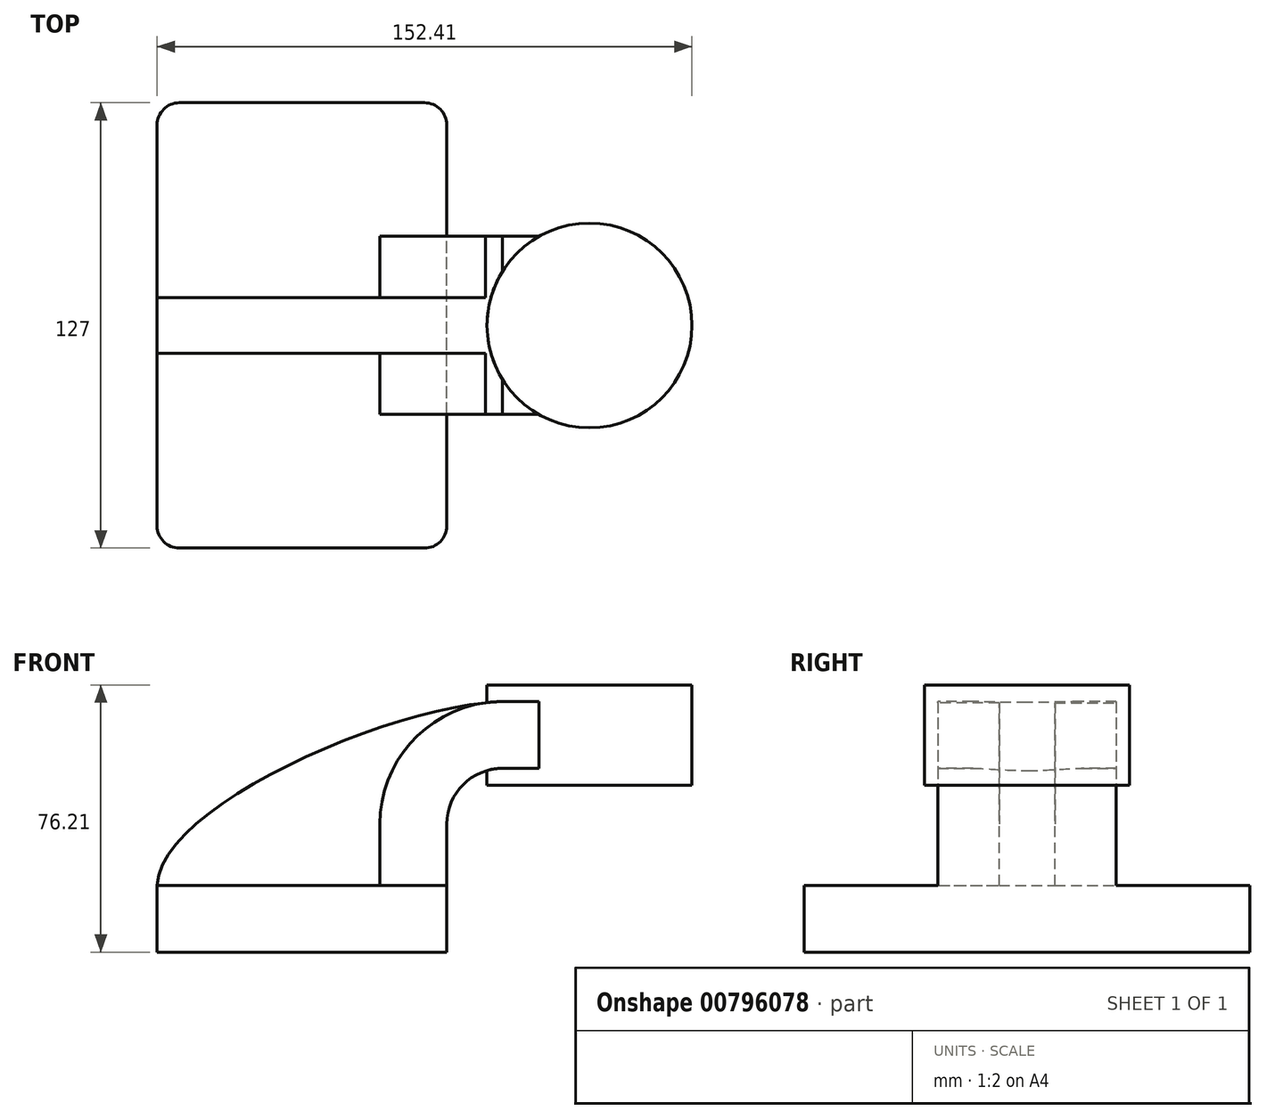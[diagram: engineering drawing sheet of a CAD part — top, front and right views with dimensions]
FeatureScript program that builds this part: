
annotation { "Feature Type Name" : "Feature", "Feature Type Description" : "" }
export const myFeature = defineFeature(function(context is Context, id is Id, definition is map)
    precondition{}
    {
        {
            var Q0;
            Q0=qCreatedBy(makeId("Front.planeOp"),FACE);
            var sketch = newSketch(context, id + "F0", { "sketchPlane" : qUnion([Q0])});
            skLineSegment(sketch, "E0.bottom", {"start": v(-41.27, -9.52) * mm, "end": v(41.28, -9.52) * mm});
            skLineSegment(sketch, "E0.top", {"start": v(-41.27, 9.52) * mm, "end": v(41.28, 9.52) * mm});
            skLineSegment(sketch, "E0.left", {"start": v(-41.27, -9.52) * mm, "end": v(-41.27, 9.52) * mm});
            skLineSegment(sketch, "E0.right", {"start": v(41.28, -9.52) * mm, "end": v(41.28, 9.52) * mm});
            skPoint(sketch, "E0.middle", {"position": v(0, 0) * mm});
            skLineSegment(sketch, "E1.bottom", {"start": v(60.33, 38.1) * mm, "end": v(111.13, 38.1) * mm});
            skLineSegment(sketch, "E1.top", {"start": v(60.33, 66.68) * mm, "end": v(111.13, 66.68) * mm});
            skLineSegment(sketch, "E1.left", {"start": v(60.33, 38.1) * mm, "end": v(60.33, 66.68) * mm});
            skLineSegment(sketch, "E1.right", {"start": v(111.13, 38.1) * mm, "end": v(111.13, 66.68) * mm});
            skPoint(sketch, "E1.middle", {"position": v(85.72, 52.39) * mm});
            skLineSegment(sketch, "E2", {"start": v(41.27, 9.52) * mm, "end": v(41.27, 27) * mm});
            skArc(sketch, "E3", {"start": v(41.27, 27) * mm, "mid": v(45.92, 38.23) * mm, "end": v(57.15, 42.88) * mm});
            skLineSegment(sketch, "E4", {"start": v(57.15, 42.88) * mm, "end": v(81.93, 42.88) * mm});
            skLineSegment(sketch, "E5.0", {"start": v(57.15, 61.93) * mm, "end": v(81.93, 61.93) * mm});
            skArc(sketch, "E5.1", {"start": v(22.22, 27) * mm, "mid": v(32.45, 51.7) * mm, "end": v(57.15, 61.93) * mm});
            skLineSegment(sketch, "E5.2", {"start": v(22.22, 9.52) * mm, "end": v(22.22, 27) * mm});
            skLineSegment(sketch, "E6", {"start": v(81.93, 42.88) * mm, "end": v(81.93, 61.93) * mm});
            skFitSpline(sketch, "E7", {"points": [v(-41.27, 9.53) * mm, v(57.15, 61.93) * mm], "startDerivative": vector(1.94, 68.42) * mm, "endDerivative": vector(93.8, 2.88) * mm});
            skLineSegment(sketch, "E8", {"start": v(81.93, 61.93) * mm, "end": v(81.93, 66.68) * mm});
            skLineSegment(sketch, "E9", {"start": v(81.93, 42.88) * mm, "end": v(81.93, 38.1) * mm});
            skSolve(sketch);
        }
        {
            var Q0;
            Q0=makeQuery(id+"F0.imprint","IMPRINT",FACE,{"disambiguationData":[TD([[makeQuery(id+"F0.imprint","IMPRINT",EDGE,{"derivedFrom":sQuery(id+"F0.wireOp",EDGE,"E0.bottom")}),1.0]])]});
            extrude(context, id + "F1", {"entities" : qUnion([Q0]), "endBound" : BoundingType.SYMMETRIC, "depth" : 127 * mm, "offsetDistance" : 25.4 * mm});
        }
        {
            var Q0;
            {var subQ0=sQuery(id+"F0.wireOp",EDGE,"E2");Q0=makeQuery(id+"F0.imprint","IMPRINT",FACE,{"disambiguationData":[TD([[makeQuery(id+"F0.imprint","IMPRINT",EDGE,{"derivedFrom":subQ0}),1.0]])]});}
            var Q1;
            {var subQ5=sQuery(id+"F0.wireOp",EDGE,"E6");Q1=makeQuery(id+"F0.imprint","IMPRINT",FACE,{"disambiguationData":[TD([[makeQuery(id+"F0.imprint","IMPRINT",EDGE,{"derivedFrom":subQ5}),1.0]])]});}
            extrude(context, id + "F2", {"entities" : qUnion([Q0, Q1]), "operationType" : NewBodyOperationType.ADD, "endBound" : BoundingType.SYMMETRIC, "depth" : 50.8 * mm, "offsetDistance" : 25.4 * mm});
        }
        {
            var Q0;
            {var subQ3=sQuery(id+"F0.wireOp",EDGE,"E5.2");Q0=makeQuery(id+"F0.imprint","IMPRINT",FACE,{"disambiguationData":[TD([[makeQuery(id+"F0.imprint","IMPRINT",EDGE,{"derivedFrom":subQ3}),1.0]])]});}
            extrude(context, id + "F3", {"entities" : qUnion([Q0]), "operationType" : NewBodyOperationType.ADD, "endBound" : BoundingType.SYMMETRIC, "depth" : 15.88 * mm, "offsetDistance" : 25.4 * mm});
        }
        {
            var Q0;
            {var subQ0=sQuery(id+"F0.wireOp",EDGE,"E1.right");Q0=makeQuery(id+"F0.imprint","IMPRINT",FACE,{"disambiguationData":[TD([[makeQuery(id+"F0.imprint","IMPRINT",EDGE,{"derivedFrom":subQ0}),1.0]])]});}
            var Q1;
            Q1=sQuery(id+"F0.wireOp",EDGE,"E6");
            revolve(context, id + "F4", {"operationType" : NewBodyOperationType.ADD, "surfaceOperationType" : NewSurfaceOperationType.NEW, "entities" : qUnion([Q0]), "axis" : qUnion([Q1]), "revolveType" : RevolveType.FULL});
        }
        {
            var Q0;
            Q0=makeQuery(id+"F1.opExtrude","CAP_EDGE",EDGE,{"disambiguationData":[OSD([sQuery(id+"F0.wireOp",EDGE,"E0.right")])],"isStart":false});
            var Q1;
            Q1=makeQuery(id+"F1.opExtrude","CAP_EDGE",EDGE,{"disambiguationData":[OSD([sQuery(id+"F0.wireOp",EDGE,"E0.left")])],"isStart":false});
            var Q2;
            Q2=makeQuery(id+"F1.opExtrude","CAP_EDGE",EDGE,{"disambiguationData":[OSD([sQuery(id+"F0.wireOp",EDGE,"E0.right")])],"isStart":true});
            var Q3;
            Q3=makeQuery(id+"F1.opExtrude","CAP_EDGE",EDGE,{"disambiguationData":[OSD([sQuery(id+"F0.wireOp",EDGE,"E0.left")])],"isStart":true});
            fillet(context, id + "F5", {"entities" : qUnion([Q0, Q1, Q2, Q3]), "radius" : 6.35 * mm, "tangentPropagation" : true, "allowEdgeOverflow" : false});
        }
    });
